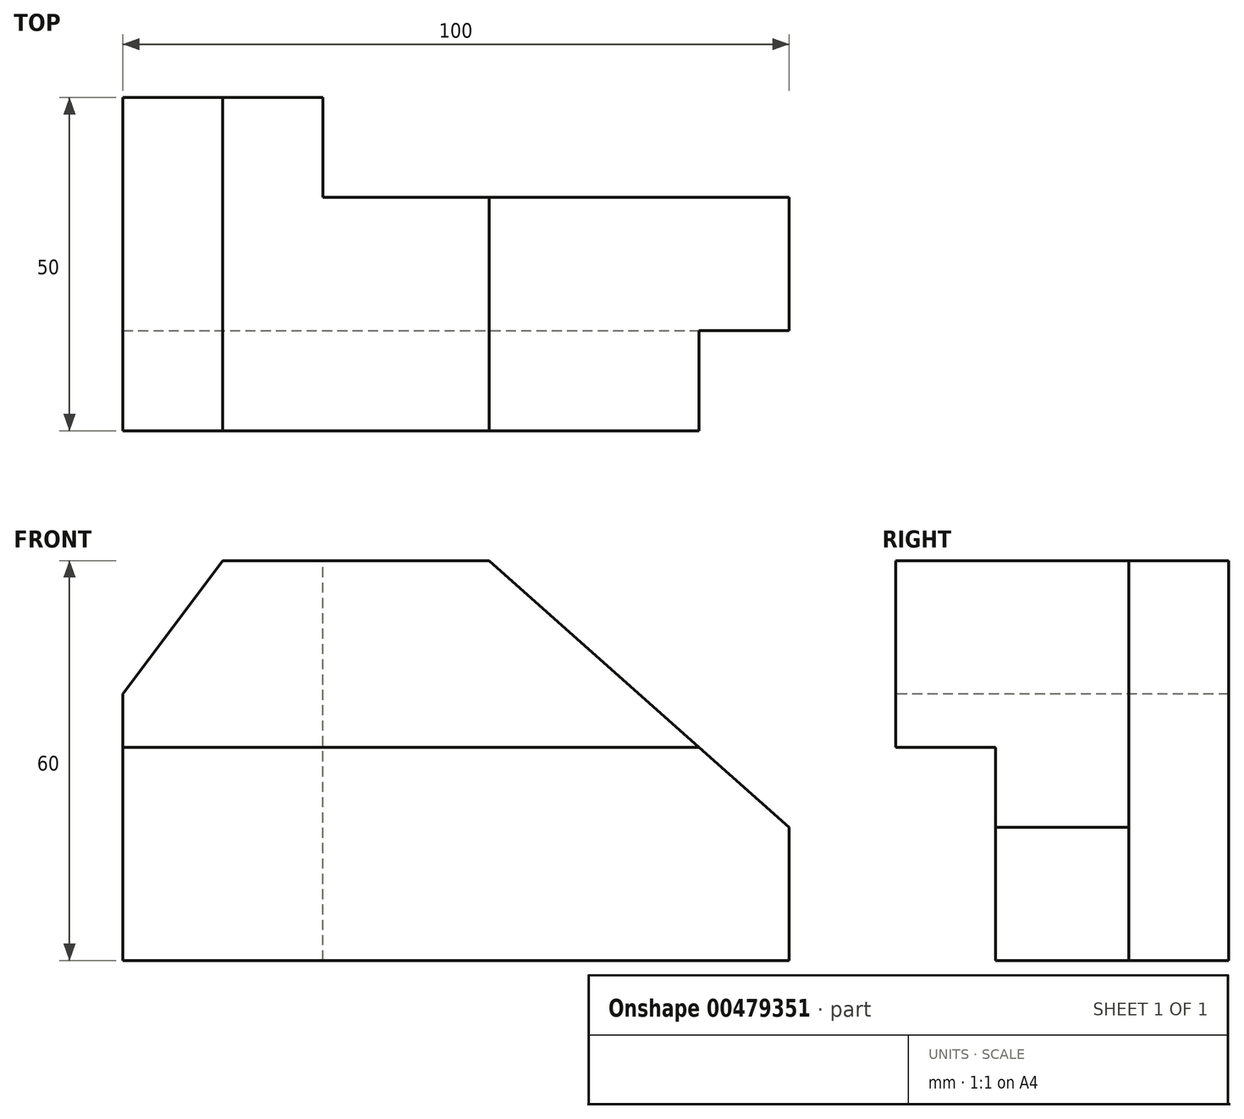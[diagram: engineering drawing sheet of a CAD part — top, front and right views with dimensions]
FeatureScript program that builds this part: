
annotation { "Feature Type Name" : "Feature", "Feature Type Description" : "" }
export const myFeature = defineFeature(function(context is Context, id is Id, definition is map)
    precondition{}
    {
        {
            var Q0;
            Q0=qCreatedBy(makeId("Top.planeOp"),FACE);
            var sketch = newSketch(context, id + "F0", { "sketchPlane" : qUnion([Q0])});
            skLineSegment(sketch, "E0.bottom", {"start": v(0, 0) * mm, "end": v(100, 0) * mm});
            skLineSegment(sketch, "E0.top", {"start": v(0, 50) * mm, "end": v(100, 50) * mm});
            skLineSegment(sketch, "E0.left", {"start": v(0, 0) * mm, "end": v(0, 50) * mm});
            skLineSegment(sketch, "E0.right", {"start": v(100, 0) * mm, "end": v(100, 50) * mm});
            skSolve(sketch);
        }
        {
            var Q0;
            Q0 = qSketchRegion(id + "F0", true);
            extrude(context, id + "F1", {"entities" : qUnion([Q0]), "depth" : 60 * mm});
        }
        {
            var Q0;
            Q0=makeQuery(id+"F1.opExtrude","SWEPT_FACE",FACE,{"disambiguationData":[OSD([sQuery(id+"F0.wireOp",EDGE,"E0.bottom")])]});
            var sketch = newSketch(context, id + "F2", { "sketchPlane" : qUnion([Q0])});
            skLineSegment(sketch, "E1.bottom", {"start": v(0, 0) * mm, "end": v(100, 0) * mm});
            skLineSegment(sketch, "E1.top", {"start": v(0, 32) * mm, "end": v(100, 32) * mm});
            skLineSegment(sketch, "E1.left", {"start": v(0, 0) * mm, "end": v(0, 32) * mm});
            skLineSegment(sketch, "E1.right", {"start": v(100, 0) * mm, "end": v(100, 32) * mm});
            skSolve(sketch);
        }
        {
            var Q0;
            Q0 = qSketchRegion(id + "F2", true);
            extrude(context, id + "F3", {"entities" : qUnion([Q0]), "operationType" : NewBodyOperationType.REMOVE, "oppositeDirection" : true, "depth" : 15 * mm});
        }
        {
            var Q0;
            Q0=makeQuery(id+"F1.opExtrude","SWEPT_FACE",FACE,{"disambiguationData":[OSD([sQuery(id+"F0.wireOp",EDGE,"E0.bottom")])]});
            var sketch = newSketch(context, id + "F4", { "sketchPlane" : qUnion([Q0])});
            skLineSegment(sketch, "E2", {"start": v(0, 60) * mm, "end": v(0, 40) * mm});
            skLineSegment(sketch, "E3", {"start": v(0, 60) * mm, "end": v(15, 60) * mm});
            skLineSegment(sketch, "E4", {"start": v(15, 60) * mm, "end": v(0, 40) * mm});
            skSolve(sketch);
        }
        {
            var Q0;
            Q0 = qSketchRegion(id + "F4", true);
            extrude(context, id + "F5", {"entities" : qUnion([Q0]), "operationType" : NewBodyOperationType.REMOVE, "endBound" : BoundingType.THROUGH_ALL, "oppositeDirection" : true, "depth" : 25 * mm});
        }
        {
            var Q0;
            Q0=makeQuery(id+"F1.opExtrude","CAP_FACE",FACE,{"disambiguationData":[OSD([sQuery(id+"F0.wireOp",EDGE,"E0.bottom"),sQuery(id+"F0.wireOp",EDGE,"E0.top"),sQuery(id+"F0.wireOp",EDGE,"E0.left"),sQuery(id+"F0.wireOp",EDGE,"E0.right")])],"isStart":false});
            var sketch = newSketch(context, id + "F6", { "sketchPlane" : qUnion([Q0])});
            skLineSegment(sketch, "E5.bottom", {"start": v(100, 50) * mm, "end": v(30, 50) * mm});
            skLineSegment(sketch, "E5.top", {"start": v(100, 35) * mm, "end": v(30, 35) * mm});
            skLineSegment(sketch, "E5.left", {"start": v(100, 50) * mm, "end": v(100, 35) * mm});
            skLineSegment(sketch, "E5.right", {"start": v(30, 50) * mm, "end": v(30, 35) * mm});
            skSolve(sketch);
        }
        {
            var Q0;
            Q0 = qSketchRegion(id + "F6", true);
            extrude(context, id + "F7", {"entities" : qUnion([Q0]), "operationType" : NewBodyOperationType.REMOVE, "endBound" : BoundingType.THROUGH_ALL, "oppositeDirection" : true, "depth" : 25 * mm});
        }
        {
            var Q0;
            Q0=makeQuery(id+"F1.opExtrude","SWEPT_FACE",FACE,{"disambiguationData":[OSD([sQuery(id+"F0.wireOp",EDGE,"E0.top")])]});
            var sketch = newSketch(context, id + "F8", { "sketchPlane" : qUnion([Q0])});
            skLineSegment(sketch, "E6", {"start": v(-100, 60) * mm, "end": v(-100, 20) * mm});
            skLineSegment(sketch, "E7", {"start": v(-100, 60) * mm, "end": v(-55, 60) * mm});
            skLineSegment(sketch, "E8", {"start": v(-55, 60) * mm, "end": v(-100, 20) * mm});
            skSolve(sketch);
        }
        {
            var Q0;
            Q0 = qSketchRegion(id + "F8", true);
            extrude(context, id + "F9", {"entities" : qUnion([Q0]), "operationType" : NewBodyOperationType.REMOVE, "endBound" : BoundingType.THROUGH_ALL, "oppositeDirection" : true, "depth" : 25 * mm});
        }
    });
